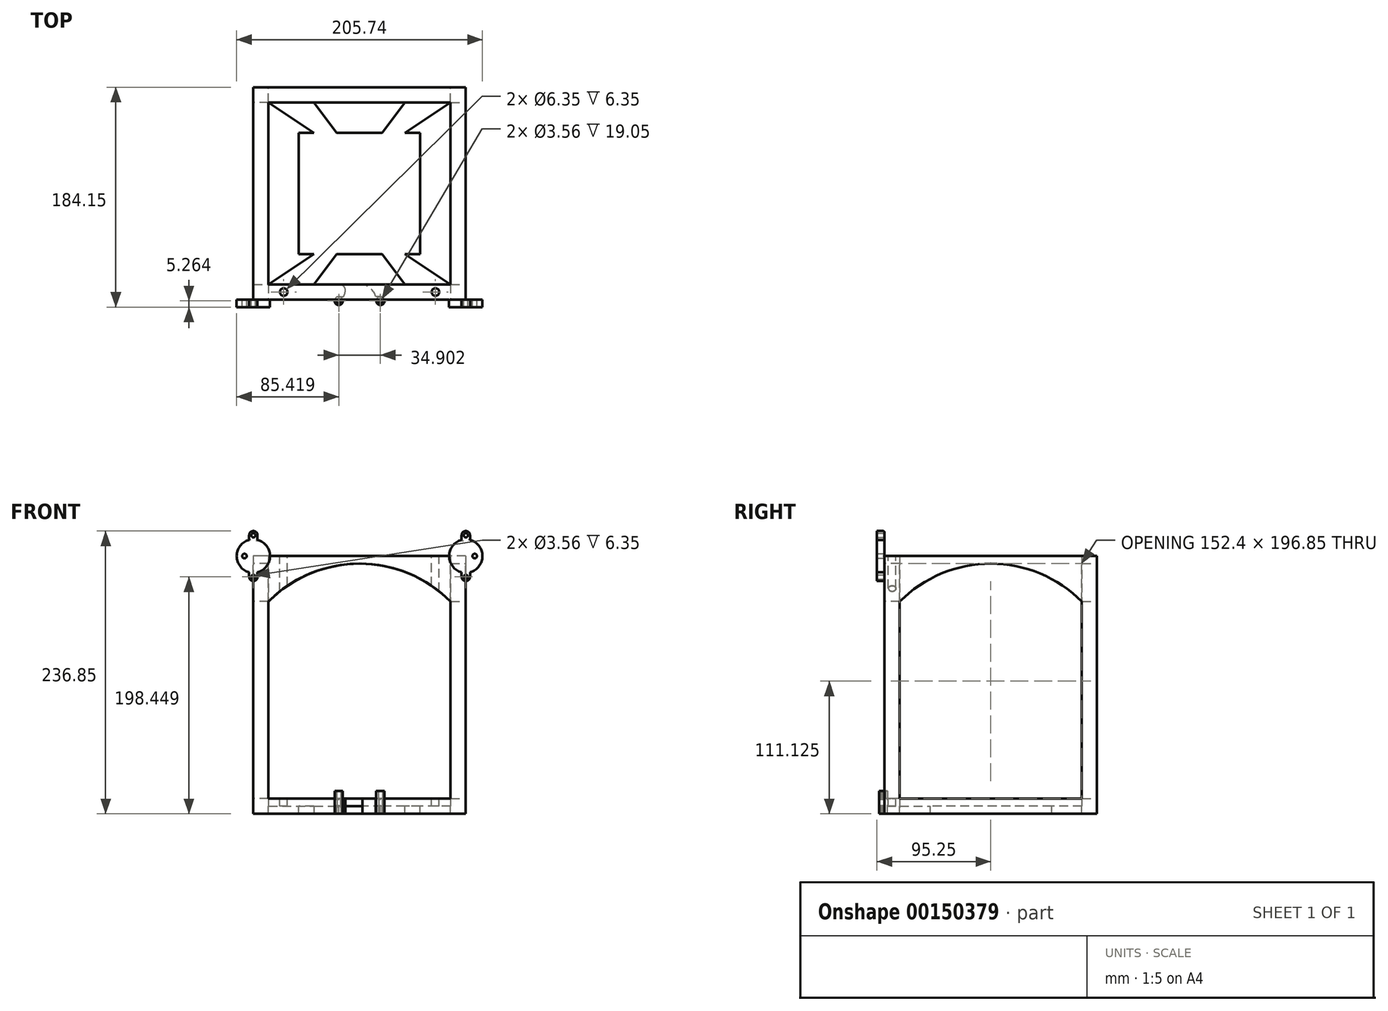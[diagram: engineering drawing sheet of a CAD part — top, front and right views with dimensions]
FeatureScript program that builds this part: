
annotation { "Feature Type Name" : "Feature", "Feature Type Description" : "" }
export const myFeature = defineFeature(function(context is Context, id is Id, definition is map)
    precondition{}
    {
        {
            var Q0;
            Q0=qCreatedBy(makeId("Top.planeOp"),FACE);
            var sketch = newSketch(context, id + "F0", { "sketchPlane" : qUnion([Q0])});
            skLineSegment(sketch, "E0.bottom", {"start": v(50.8, 50.8) * mm, "end": v(-50.8, 50.8) * mm});
            skLineSegment(sketch, "E0.top", {"start": v(50.8, -50.8) * mm, "end": v(-50.8, -50.8) * mm});
            skLineSegment(sketch, "E0.left", {"start": v(50.8, 50.8) * mm, "end": v(50.8, -50.8) * mm});
            skLineSegment(sketch, "E0.right", {"start": v(-50.8, 50.8) * mm, "end": v(-50.8, -50.8) * mm});
            skPoint(sketch, "E0.middle", {"position": v(0, 0) * mm});
            skSolve(sketch);
        }
        {
            var Q0;
            Q0 = qSketchRegion(id + "F0", true);
            extrude(context, id + "F1", {"entities" : qUnion([Q0]), "oppositeDirection" : true, "depth" : 6.35 * mm});
        }
        {
            var Q0;
            Q0=qCreatedBy(makeId("Right.planeOp"),FACE);
            var sketch = newSketch(context, id + "F2", { "sketchPlane" : qUnion([Q0])});
            skLineSegment(sketch, "E1.bottom", {"start": v(-76.2, 6.35) * mm, "end": v(-88.9, 6.35) * mm});
            skLineSegment(sketch, "E1.top", {"start": v(-76.2, -6.35) * mm, "end": v(-88.9, -6.35) * mm});
            skLineSegment(sketch, "E1.left", {"start": v(-76.2, 6.35) * mm, "end": v(-76.2, -6.35) * mm});
            skLineSegment(sketch, "E1.right", {"start": v(-88.9, 6.35) * mm, "end": v(-88.9, -6.35) * mm});
            skPoint(sketch, "E1.middle", {"position": v(-82.55, 0) * mm});
            skSolve(sketch);
        }
        {
            var Q0;
            Q0 = qSketchRegion(id + "F2", true);
            extrude(context, id + "F3", {"entities" : qUnion([Q0]), "endBound" : BoundingType.SYMMETRIC, "depth" : 177.8 * mm});
        }
        {
            var Q0;
            Q0=makeQuery(id+"F3.opExtrude","SWEPT_BODY",BODY,{"disambiguationData":[OSD([sQuery(id+"F2.wireOp",EDGE,"E1.bottom"),sQuery(id+"F2.wireOp",EDGE,"E1.top"),sQuery(id+"F2.wireOp",EDGE,"E1.left"),sQuery(id+"F2.wireOp",EDGE,"E1.right")])]});
            var Q1;
            Q1=qCreatedBy(makeId("Front.planeOp"),FACE);
            mirror(context, id + "F4", {"entities" : qUnion([Q0]), "mirrorPlane" : qUnion([Q1])});
        }
        {
            var Q0;
            Q0=qCreatedBy(makeId("Front.planeOp"),FACE);
            var sketch = newSketch(context, id + "F5", { "sketchPlane" : qUnion([Q0])});
            skLineSegment(sketch, "E2", {"start": v(76.2, 6.35) * mm, "end": v(76.2, -6.35) * mm});
            skLineSegment(sketch, "E3", {"start": v(76.2, -6.35) * mm, "end": v(88.9, -6.35) * mm});
            skLineSegment(sketch, "E4", {"start": v(88.9, -6.35) * mm, "end": v(88.9, 6.35) * mm});
            skLineSegment(sketch, "E5", {"start": v(88.9, 6.35) * mm, "end": v(76.2, 6.35) * mm});
            skSolve(sketch);
        }
        {
            var Q0;
            Q0 = qSketchRegion(id + "F5", true);
            extrude(context, id + "F6", {"entities" : qUnion([Q0]), "endBound" : BoundingType.SYMMETRIC, "depth" : 152.4 * mm});
        }
        {
            var Q0;
            Q0=makeQuery(id+"F6.opExtrude","SWEPT_BODY",BODY,{"disambiguationData":[OSD([sQuery(id+"F5.wireOp",EDGE,"E2"),sQuery(id+"F5.wireOp",EDGE,"E3"),sQuery(id+"F5.wireOp",EDGE,"E4"),sQuery(id+"F5.wireOp",EDGE,"E5")])]});
            var Q1;
            Q1=qCreatedBy(makeId("Right.planeOp"),FACE);
            mirror(context, id + "F7", {"entities" : qUnion([Q0]), "mirrorPlane" : qUnion([Q1])});
        }
        {
            var Q0;
            Q0=makeQuery(id+"F1.opExtrude","SWEPT_FACE",FACE,{"disambiguationData":[OSD([sQuery(id+"F0.wireOp",EDGE,"E0.top")])]});
            var sketch = newSketch(context, id + "F8", { "sketchPlane" : qUnion([Q0])});
            skLineSegment(sketch, "E6", {"start": v(-38.1, 0) * mm, "end": v(-38.1, -6.35) * mm});
            skLineSegment(sketch, "E7", {"start": v(-38.1, -6.35) * mm, "end": v(-19.05, -6.35) * mm});
            skLineSegment(sketch, "E8", {"start": v(-19.05, -6.35) * mm, "end": v(-19.05, 0) * mm});
            skLineSegment(sketch, "E9", {"start": v(-19.05, 0) * mm, "end": v(-38.1, 0) * mm});
            skLineSegment(sketch, "E10.MirrorCS", {"start": v(19.05, -6.35) * mm, "end": v(19.05, 0) * mm, "construction": true});
            skLineSegment(sketch, "E11.MirrorCS", {"start": v(19.05, 0) * mm, "end": v(38.1, 0) * mm, "construction": true});
            skLineSegment(sketch, "E12.MirrorCS", {"start": v(38.1, 0) * mm, "end": v(38.1, -6.35) * mm, "construction": true});
            skLineSegment(sketch, "E13.MirrorCS", {"start": v(38.1, -6.35) * mm, "end": v(19.05, -6.35) * mm, "construction": true});
            skSolve(sketch);
        }
        {
            var Q0;
            Q0=makeQuery(id+"F3.opExtrude","SWEPT_FACE",FACE,{"disambiguationData":[OSD([sQuery(id+"F2.wireOp",EDGE,"E1.left")])]});
            var sketch = newSketch(context, id + "F9", { "sketchPlane" : qUnion([Q0])});
            skLineSegment(sketch, "E14.bottom", {"start": v(-76.2, -6.35) * mm, "end": v(-38.1, -6.35) * mm, "construction": true});
            skLineSegment(sketch, "E14.top", {"start": v(-76.2, 0) * mm, "end": v(-38.1, 0) * mm, "construction": true});
            skLineSegment(sketch, "E14.left", {"start": v(-76.2, -6.35) * mm, "end": v(-76.2, 0) * mm, "construction": true});
            skLineSegment(sketch, "E14.right", {"start": v(-38.1, -6.35) * mm, "end": v(-38.1, 0) * mm, "construction": true});
            skLineSegment(sketch, "E15.MirrorCS", {"start": v(76.2, 0) * mm, "end": v(38.1, 0) * mm});
            skLineSegment(sketch, "E16.MirrorCS", {"start": v(38.1, -6.35) * mm, "end": v(38.1, 0) * mm});
            skLineSegment(sketch, "E17.MirrorCS", {"start": v(76.2, -6.35) * mm, "end": v(38.1, -6.35) * mm});
            skLineSegment(sketch, "E18.MirrorCS", {"start": v(76.2, -6.35) * mm, "end": v(76.2, 0) * mm});
            skSolve(sketch);
        }
        {
            var Q0;
            Q0=makeQuery(id+"F9.imprint","IMPRINT",FACE,{"disambiguationData":[TD([[makeQuery(id+"F9.imprint","IMPRINT",EDGE,{"derivedFrom":sQuery(id+"F9.wireOp",EDGE,"E15.MirrorCS")}),1.0]])]});
            var Q1;
            Q1=makeQuery(id+"F8.imprint","IMPRINT",FACE,{"disambiguationData":[TD([[makeQuery(id+"F8.imprint","IMPRINT",EDGE,{"derivedFrom":sQuery(id+"F8.wireOp",EDGE,"E6")}),1.0]])]});
            loft(context, id + "F10", {"sheetProfilesArray" : [{ "sheetProfileEntities" : qUnion([Q0]) }, { "sheetProfileEntities" : qUnion([Q1]) }]});
        }
        {
            var Q0;
            Q0=makeQuery(id+"F10.opLoft","SWEPT_BODY",BODY,{"disambiguationData":[OSD([makeQuery(id+"F8.imprint","IMPRINT",FACE,{"disambiguationData":[TD([[makeQuery(id+"F8.imprint","IMPRINT",EDGE,{"derivedFrom":sQuery(id+"F8.wireOp",EDGE,"E6")}),1.0]])]}),makeQuery(id+"F9.imprint","IMPRINT",FACE,{"disambiguationData":[TD([[makeQuery(id+"F9.imprint","IMPRINT",EDGE,{"derivedFrom":sQuery(id+"F9.wireOp",EDGE,"E15.MirrorCS")}),1.0]])]})])]});
            var Q1;
            Q1=qCreatedBy(makeId("Right.planeOp"),FACE);
            mirror(context, id + "F11", {"entities" : qUnion([Q0]), "mirrorPlane" : qUnion([Q1])});
        }
        {
            var Q0;
            Q0=makeQuery(id+"F11.opPattern","COPY",BODY,{"derivedFrom":makeQuery(id+"F10.opLoft","SWEPT_BODY",BODY,{"disambiguationData":[OSD([makeQuery(id+"F8.imprint","IMPRINT",FACE,{"disambiguationData":[TD([[makeQuery(id+"F8.imprint","IMPRINT",EDGE,{"derivedFrom":sQuery(id+"F8.wireOp",EDGE,"E6")}),1.0]])]}),makeQuery(id+"F9.imprint","IMPRINT",FACE,{"disambiguationData":[TD([[makeQuery(id+"F9.imprint","IMPRINT",EDGE,{"derivedFrom":sQuery(id+"F9.wireOp",EDGE,"E15.MirrorCS")}),1.0]])]})])]}),"instanceName":"1"});
            var Q1;
            Q1=makeQuery(id+"F10.opLoft","SWEPT_BODY",BODY,{"disambiguationData":[OSD([makeQuery(id+"F8.imprint","IMPRINT",FACE,{"disambiguationData":[TD([[makeQuery(id+"F8.imprint","IMPRINT",EDGE,{"derivedFrom":sQuery(id+"F8.wireOp",EDGE,"E6")}),1.0]])]}),makeQuery(id+"F9.imprint","IMPRINT",FACE,{"disambiguationData":[TD([[makeQuery(id+"F9.imprint","IMPRINT",EDGE,{"derivedFrom":sQuery(id+"F9.wireOp",EDGE,"E15.MirrorCS")}),1.0]])]})])]});
            var Q2;
            Q2=qCreatedBy(makeId("Front.planeOp"),FACE);
            mirror(context, id + "F12", {"entities" : qUnion([Q0, Q1]), "mirrorPlane" : qUnion([Q2])});
        }
        {
            var Q0;
            Q0=makeQuery(id+"F1.opExtrude","SWEPT_BODY",BODY,{"disambiguationData":[OSD([sQuery(id+"F0.wireOp",EDGE,"E0.bottom"),sQuery(id+"F0.wireOp",EDGE,"E0.top"),sQuery(id+"F0.wireOp",EDGE,"E0.left"),sQuery(id+"F0.wireOp",EDGE,"E0.right")])]});
            var Q1;
            Q1=makeQuery(id+"F7.opPattern","COPY",BODY,{"derivedFrom":makeQuery(id+"F6.opExtrude","SWEPT_BODY",BODY,{"disambiguationData":[OSD([sQuery(id+"F5.wireOp",EDGE,"E2"),sQuery(id+"F5.wireOp",EDGE,"E3"),sQuery(id+"F5.wireOp",EDGE,"E4"),sQuery(id+"F5.wireOp",EDGE,"E5")])]}),"instanceName":"1"});
            var Q2;
            Q2=makeQuery(id+"F12.opPattern","COPY",BODY,{"derivedFrom":makeQuery(id+"F10.opLoft","SWEPT_BODY",BODY,{"disambiguationData":[OSD([makeQuery(id+"F8.imprint","IMPRINT",FACE,{"disambiguationData":[TD([[makeQuery(id+"F8.imprint","IMPRINT",EDGE,{"derivedFrom":sQuery(id+"F8.wireOp",EDGE,"E6")}),1.0]])]}),makeQuery(id+"F9.imprint","IMPRINT",FACE,{"disambiguationData":[TD([[makeQuery(id+"F9.imprint","IMPRINT",EDGE,{"derivedFrom":sQuery(id+"F9.wireOp",EDGE,"E15.MirrorCS")}),1.0]])]})])]}),"instanceName":"1"});
            var Q3;
            Q3=makeQuery(id+"F4.opPattern","COPY",BODY,{"derivedFrom":makeQuery(id+"F3.opExtrude","SWEPT_BODY",BODY,{"disambiguationData":[OSD([sQuery(id+"F2.wireOp",EDGE,"E1.bottom"),sQuery(id+"F2.wireOp",EDGE,"E1.top"),sQuery(id+"F2.wireOp",EDGE,"E1.left"),sQuery(id+"F2.wireOp",EDGE,"E1.right")])]}),"instanceName":"1"});
            var Q4;
            Q4=makeQuery(id+"F3.opExtrude","SWEPT_BODY",BODY,{"disambiguationData":[OSD([sQuery(id+"F2.wireOp",EDGE,"E1.bottom"),sQuery(id+"F2.wireOp",EDGE,"E1.top"),sQuery(id+"F2.wireOp",EDGE,"E1.left"),sQuery(id+"F2.wireOp",EDGE,"E1.right")])]});
            var Q5;
            Q5=makeQuery(id+"F6.opExtrude","SWEPT_BODY",BODY,{"disambiguationData":[OSD([sQuery(id+"F5.wireOp",EDGE,"E2"),sQuery(id+"F5.wireOp",EDGE,"E3"),sQuery(id+"F5.wireOp",EDGE,"E4"),sQuery(id+"F5.wireOp",EDGE,"E5")])]});
            var Q6;
            Q6=makeQuery(id+"F11.opPattern","COPY",BODY,{"derivedFrom":makeQuery(id+"F10.opLoft","SWEPT_BODY",BODY,{"disambiguationData":[OSD([makeQuery(id+"F8.imprint","IMPRINT",FACE,{"disambiguationData":[TD([[makeQuery(id+"F8.imprint","IMPRINT",EDGE,{"derivedFrom":sQuery(id+"F8.wireOp",EDGE,"E6")}),1.0]])]}),makeQuery(id+"F9.imprint","IMPRINT",FACE,{"disambiguationData":[TD([[makeQuery(id+"F9.imprint","IMPRINT",EDGE,{"derivedFrom":sQuery(id+"F9.wireOp",EDGE,"E15.MirrorCS")}),1.0]])]})])]}),"instanceName":"1"});
            var Q7;
            Q7=makeQuery(id+"F10.opLoft","SWEPT_BODY",BODY,{"disambiguationData":[OSD([makeQuery(id+"F8.imprint","IMPRINT",FACE,{"disambiguationData":[TD([[makeQuery(id+"F8.imprint","IMPRINT",EDGE,{"derivedFrom":sQuery(id+"F8.wireOp",EDGE,"E6")}),1.0]])]}),makeQuery(id+"F9.imprint","IMPRINT",FACE,{"disambiguationData":[TD([[makeQuery(id+"F9.imprint","IMPRINT",EDGE,{"derivedFrom":sQuery(id+"F9.wireOp",EDGE,"E15.MirrorCS")}),1.0]])]})])]});
            var Q8;
            Q8=makeQuery(id+"F12.opPattern","COPY",BODY,{"derivedFrom":makeQuery(id+"F11.opPattern","COPY",BODY,{"derivedFrom":makeQuery(id+"F10.opLoft","SWEPT_BODY",BODY,{"disambiguationData":[OSD([makeQuery(id+"F8.imprint","IMPRINT",FACE,{"disambiguationData":[TD([[makeQuery(id+"F8.imprint","IMPRINT",EDGE,{"derivedFrom":sQuery(id+"F8.wireOp",EDGE,"E6")}),1.0]])]}),makeQuery(id+"F9.imprint","IMPRINT",FACE,{"disambiguationData":[TD([[makeQuery(id+"F9.imprint","IMPRINT",EDGE,{"derivedFrom":sQuery(id+"F9.wireOp",EDGE,"E15.MirrorCS")}),1.0]])]})])]}),"instanceName":"1"}),"instanceName":"1"});
            booleanBodies(context, id + "F13", {"operationType" : BooleanOperationType.UNION, "tools" : qUnion([Q0, Q1, Q2, Q3, Q4, Q5, Q6, Q7, Q8])});
        }
        {
            var Q0;
            {var subQ0=makeQuery(id+"F6.opExtrude","SWEPT_FACE",FACE,{"disambiguationData":[OSD([sQuery(id+"F5.wireOp",EDGE,"E5")])]});var subQ1=makeQuery(id+"F3.opExtrude","SWEPT_FACE",FACE,{"disambiguationData":[OSD([sQuery(id+"F2.wireOp",EDGE,"E1.bottom")])]});Q0=makeQuery(id+"F13.opBoolean","MERGE",FACE,{"derivedFrom":[subQ1,makeQuery(id+"F4.opPattern","COPY",FACE,{"derivedFrom":subQ1,"instanceName":"1"}),subQ0,makeQuery(id+"F7.opPattern","COPY",FACE,{"derivedFrom":subQ0,"instanceName":"1"})]});}
            var sketch = newSketch(context, id + "F14", { "sketchPlane" : qUnion([Q0])});
            skLineSegment(sketch, "E19.bottom", {"start": v(-76.2, 76.2) * mm, "end": v(-88.9, 76.2) * mm});
            skLineSegment(sketch, "E19.top", {"start": v(-76.2, 88.9) * mm, "end": v(-88.9, 88.9) * mm});
            skLineSegment(sketch, "E19.left", {"start": v(-76.2, 76.2) * mm, "end": v(-76.2, 88.9) * mm});
            skLineSegment(sketch, "E19.right", {"start": v(-88.9, 76.2) * mm, "end": v(-88.9, 88.9) * mm});
            skLineSegment(sketch, "E20.bottom", {"start": v(76.2, 76.2) * mm, "end": v(88.9, 76.2) * mm});
            skLineSegment(sketch, "E20.top", {"start": v(76.2, 88.9) * mm, "end": v(88.9, 88.9) * mm});
            skLineSegment(sketch, "E20.left", {"start": v(76.2, 76.2) * mm, "end": v(76.2, 88.9) * mm});
            skLineSegment(sketch, "E20.right", {"start": v(88.9, 76.2) * mm, "end": v(88.9, 88.9) * mm});
            skLineSegment(sketch, "E21.bottom", {"start": v(76.2, -76.2) * mm, "end": v(88.9, -76.2) * mm});
            skLineSegment(sketch, "E21.top", {"start": v(76.2, -88.9) * mm, "end": v(88.9, -88.9) * mm});
            skLineSegment(sketch, "E21.left", {"start": v(76.2, -76.2) * mm, "end": v(76.2, -88.9) * mm});
            skLineSegment(sketch, "E21.right", {"start": v(88.9, -76.2) * mm, "end": v(88.9, -88.9) * mm});
            skLineSegment(sketch, "E22.bottom", {"start": v(-88.9, -88.9) * mm, "end": v(-76.2, -88.9) * mm});
            skLineSegment(sketch, "E22.top", {"start": v(-88.9, -76.2) * mm, "end": v(-76.2, -76.2) * mm});
            skLineSegment(sketch, "E22.left", {"start": v(-88.9, -88.9) * mm, "end": v(-88.9, -76.2) * mm});
            skLineSegment(sketch, "E22.right", {"start": v(-76.2, -88.9) * mm, "end": v(-76.2, -76.2) * mm});
            skSolve(sketch);
        }
        {
            var Q0;
            Q0 = qSketchRegion(id + "F14", true);
            extrude(context, id + "F15", {"entities" : qUnion([Q0]), "operationType" : NewBodyOperationType.ADD, "depth" : 203.2 * mm});
        }
        {
            var Q0;
            {var subQ0=makeQuery(id+"F3.opExtrude","CAP_FACE",FACE,{"disambiguationData":[OSD([sQuery(id+"F2.wireOp",EDGE,"E1.bottom"),sQuery(id+"F2.wireOp",EDGE,"E1.top"),sQuery(id+"F2.wireOp",EDGE,"E1.left"),sQuery(id+"F2.wireOp",EDGE,"E1.right")])],"isStart":true});Q0=makeQuery(id+"F15.boolean.opBoolean","MERGE",FACE,{"derivedFrom":[makeQuery(id+"F13.opBoolean","MERGE",FACE,{"derivedFrom":[subQ0,makeQuery(id+"F4.opPattern","COPY",FACE,{"derivedFrom":subQ0,"instanceName":"1"}),makeQuery(id+"F7.opPattern","COPY",FACE,{"derivedFrom":makeQuery(id+"F6.opExtrude","SWEPT_FACE",FACE,{"disambiguationData":[OSD([sQuery(id+"F5.wireOp",EDGE,"E4")])]}),"instanceName":"1"})]}),makeQuery(id+"F15.opExtrude","SWEPT_FACE",FACE,{"disambiguationData":[OSD([sQuery(id+"F14.wireOp",EDGE,"E19.right")])]}),makeQuery(id+"F15.opExtrude","SWEPT_FACE",FACE,{"disambiguationData":[OSD([sQuery(id+"F14.wireOp",EDGE,"E22.left")])]})]});}
            var sketch = newSketch(context, id + "F16", { "sketchPlane" : qUnion([Q0])});
            skArc(sketch, "E23", {"start": v(76.2, 171.45) * mm, "mid": v(0, 203.2) * mm, "end": v(-76.2, 171.45) * mm});
            skLineSegment(sketch, "E24", {"start": v(-76.2, 209.55) * mm, "end": v(76.2, 209.55) * mm});
            skLineSegment(sketch, "E25", {"start": v(76.2, 209.55) * mm, "end": v(76.2, 171.45) * mm});
            skLineSegment(sketch, "E26", {"start": v(-76.2, 209.55) * mm, "end": v(-76.2, 171.45) * mm});
            skSolve(sketch);
        }
        {
            var Q0;
            Q0 = qSketchRegion(id + "F16", true);
            extrude(context, id + "F17", {"entities" : qUnion([Q0]), "oppositeDirection" : true, "depth" : 12.7 * mm});
        }
        {
            var Q0;
            Q0=makeQuery(id+"F17.opExtrude","SWEPT_BODY",BODY,{"disambiguationData":[OSD([sQuery(id+"F16.wireOp",EDGE,"E23"),sQuery(id+"F16.wireOp",EDGE,"E24"),sQuery(id+"F16.wireOp",EDGE,"E25"),sQuery(id+"F16.wireOp",EDGE,"E26")])]});
            var Q1;
            Q1=qCreatedBy(makeId("Right.planeOp"),FACE);
            mirror(context, id + "F18", {"operationType" : NewBodyOperationType.ADD, "entities" : qUnion([Q0]), "mirrorPlane" : qUnion([Q1])});
        }
        {
            var Q0;
            Q0=makeQuery(id+"F15.boolean.opBoolean","MERGE",FACE,{"derivedFrom":[makeQuery(id+"F4.opPattern","COPY",FACE,{"derivedFrom":makeQuery(id+"F3.opExtrude","SWEPT_FACE",FACE,{"disambiguationData":[OSD([sQuery(id+"F2.wireOp",EDGE,"E1.right")])]}),"instanceName":"1"}),makeQuery(id+"F15.opExtrude","SWEPT_FACE",FACE,{"disambiguationData":[OSD([sQuery(id+"F14.wireOp",EDGE,"E19.top")])]}),makeQuery(id+"F15.opExtrude","SWEPT_FACE",FACE,{"disambiguationData":[OSD([sQuery(id+"F14.wireOp",EDGE,"E20.top")])]})]});
            var sketch = newSketch(context, id + "F19", { "sketchPlane" : qUnion([Q0])});
            skArc(sketch, "E27", {"start": v(76.2, 171.45) * mm, "mid": v(0, 203.2) * mm, "end": v(-76.2, 171.45) * mm});
            skLineSegment(sketch, "E28", {"start": v(-76.2, 171.45) * mm, "end": v(-76.2, 209.55) * mm});
            skLineSegment(sketch, "E29", {"start": v(-76.2, 209.55) * mm, "end": v(76.2, 209.55) * mm});
            skLineSegment(sketch, "E30", {"start": v(76.2, 209.55) * mm, "end": v(76.2, 171.45) * mm});
            skSolve(sketch);
        }
        {
            var Q0;
            Q0 = qSketchRegion(id + "F19", true);
            extrude(context, id + "F20", {"entities" : qUnion([Q0]), "oppositeDirection" : true, "depth" : 12.7 * mm});
        }
        {
            var Q0;
            Q0=makeQuery(id+"F20.opExtrude","SWEPT_BODY",BODY,{"disambiguationData":[OSD([sQuery(id+"F19.wireOp",EDGE,"E27"),sQuery(id+"F19.wireOp",EDGE,"E28"),sQuery(id+"F19.wireOp",EDGE,"E29"),sQuery(id+"F19.wireOp",EDGE,"E30")])]});
            var Q1;
            Q1=qCreatedBy(makeId("Front.planeOp"),FACE);
            mirror(context, id + "F21", {"operationType" : NewBodyOperationType.ADD, "entities" : qUnion([Q0]), "mirrorPlane" : qUnion([Q1])});
        }
        {
            var Q0;
            {var subQ0=makeQuery(id+"F20.opExtrude","SWEPT_FACE",FACE,{"disambiguationData":[OSD([sQuery(id+"F19.wireOp",EDGE,"E29")])]});var subQ1=makeQuery(id+"F17.opExtrude","SWEPT_FACE",FACE,{"disambiguationData":[OSD([sQuery(id+"F16.wireOp",EDGE,"E24")])]});Q0=makeQuery(id+"F21.boolean.opBoolean","MERGE",FACE,{"derivedFrom":[makeQuery(id+"F18.boolean.opBoolean","MERGE",FACE,{"derivedFrom":[makeQuery(id+"F15.opExtrude","CAP_FACE",FACE,{"disambiguationData":[OSD([sQuery(id+"F14.wireOp",EDGE,"E19.bottom"),sQuery(id+"F14.wireOp",EDGE,"E19.top"),sQuery(id+"F14.wireOp",EDGE,"E19.left"),sQuery(id+"F14.wireOp",EDGE,"E19.right")])],"isStart":false}),makeQuery(id+"F15.opExtrude","CAP_FACE",FACE,{"disambiguationData":[OSD([sQuery(id+"F14.wireOp",EDGE,"E22.bottom"),sQuery(id+"F14.wireOp",EDGE,"E22.top"),sQuery(id+"F14.wireOp",EDGE,"E22.left"),sQuery(id+"F14.wireOp",EDGE,"E22.right")])],"isStart":false}),subQ1]}),makeQuery(id+"F18.boolean.opBoolean","MERGE",FACE,{"derivedFrom":[makeQuery(id+"F15.opExtrude","CAP_FACE",FACE,{"disambiguationData":[OSD([sQuery(id+"F14.wireOp",EDGE,"E20.bottom"),sQuery(id+"F14.wireOp",EDGE,"E20.top"),sQuery(id+"F14.wireOp",EDGE,"E20.left"),sQuery(id+"F14.wireOp",EDGE,"E20.right")])],"isStart":false}),makeQuery(id+"F15.opExtrude","CAP_FACE",FACE,{"disambiguationData":[OSD([sQuery(id+"F14.wireOp",EDGE,"E21.bottom"),sQuery(id+"F14.wireOp",EDGE,"E21.top"),sQuery(id+"F14.wireOp",EDGE,"E21.left"),sQuery(id+"F14.wireOp",EDGE,"E21.right")])],"isStart":false}),makeQuery(id+"F18.opPattern","COPY",FACE,{"derivedFrom":subQ1,"instanceName":"1"})]}),subQ0,makeQuery(id+"F21.opPattern","COPY",FACE,{"derivedFrom":subQ0,"instanceName":"1"})]});}
            var sketch = newSketch(context, id + "F22", { "sketchPlane" : qUnion([Q0])});
            skCircle(sketch, "E31", {"center": v(-63.5, -82.55) * mm, "radius": 3.18 * mm});
            skCircle(sketch, "E32", {"center": v(63.5, -82.55) * mm, "radius": 3.18 * mm});
            skLineSegment(sketch, "E33", {"start": v(-63.5, -82.55) * mm, "end": v(63.5, -82.55) * mm, "construction": true});
            skLineSegment(sketch, "E34", {"start": v(63.5, -82.55) * mm, "end": v(0, 0) * mm, "construction": true});
            skLineSegment(sketch, "E35", {"start": v(0, 0) * mm, "end": v(-63.5, -82.55) * mm, "construction": true});
            skLineSegment(sketch, "E36", {"start": v(0, -76.2) * mm, "end": v(0, -82.55) * mm, "construction": true});
            skLineSegment(sketch, "E37", {"start": v(0, -82.55) * mm, "end": v(0, -88.9) * mm, "construction": true});
            skSolve(sketch);
        }
        {
            var Q0;
            Q0 = qSketchRegion(id + "F22", true);
            extrude(context, id + "F23", {"entities" : qUnion([Q0]), "operationType" : NewBodyOperationType.REMOVE, "oppositeDirection" : true, "depth" : 209.55 * mm});
        }
        {
            var Q0;
            {var subQ0=sQuery(id+"F2.wireOp",EDGE,"E1.top");var subQ1=sQuery(id+"F0.wireOp",EDGE,"E0.top");var subQ2=makeQuery(id+"F10.opLoft","SWEPT_FACE",FACE,{"disambiguationData":[OSD([subQ1,subQ0,sQuery(id+"F2.wireOp",EDGE,"E1.left"),sQuery(id+"F8.wireOp",EDGE,"E6"),sQuery(id+"F8.wireOp",EDGE,"E7"),sQuery(id+"F8.wireOp",EDGE,"E8"),sQuery(id+"F9.wireOp",EDGE,"E16.MirrorCS"),sQuery(id+"F9.wireOp",EDGE,"E17.MirrorCS"),sQuery(id+"F9.wireOp",EDGE,"E18.MirrorCS")])]});var subQ3=makeQuery(id+"F11.opPattern","COPY",FACE,{"derivedFrom":subQ2,"instanceName":"1"});var subQ4=makeQuery(id+"F6.opExtrude","SWEPT_FACE",FACE,{"disambiguationData":[OSD([sQuery(id+"F5.wireOp",EDGE,"E3")])]});var subQ5=makeQuery(id+"F3.opExtrude","SWEPT_FACE",FACE,{"disambiguationData":[OSD([subQ0])]});Q0=makeQuery(id+"F13.opBoolean","MERGE",FACE,{"derivedFrom":[makeQuery(id+"F1.opExtrude","CAP_FACE",FACE,{"disambiguationData":[OSD([sQuery(id+"F0.wireOp",EDGE,"E0.bottom"),subQ1,sQuery(id+"F0.wireOp",EDGE,"E0.left"),sQuery(id+"F0.wireOp",EDGE,"E0.right")])],"isStart":false}),subQ5,makeQuery(id+"F4.opPattern","COPY",FACE,{"derivedFrom":subQ5,"instanceName":"1"}),subQ4,makeQuery(id+"F7.opPattern","COPY",FACE,{"derivedFrom":subQ4,"instanceName":"1"}),subQ2,subQ3,makeQuery(id+"F12.opPattern","COPY",FACE,{"derivedFrom":subQ2,"instanceName":"1"}),makeQuery(id+"F12.opPattern","COPY",FACE,{"derivedFrom":subQ3,"instanceName":"1"})]});}
            var sketch = newSketch(context, id + "F24", { "sketchPlane" : qUnion([Q0])});
            skCircle(sketch, "E38", {"center": v(0, 82.55) * mm, "radius": 1.9 * mm});
            skArc(sketch, "E39", {"start": v(13.52, 93.49) * mm, "mid": v(0, 103.96) * mm, "end": v(-13.52, 93.49) * mm});
            skArc(sketch, "E40", {"start": v(17.45, 86.49) * mm, "mid": v(20.95, 89.99) * mm, "end": v(17.45, 93.49) * mm});
            skArc(sketch, "E41", {"start": v(-17.45, 93.49) * mm, "mid": v(-20.95, 89.99) * mm, "end": v(-17.45, 86.49) * mm});
            skLineSegment(sketch, "E42", {"start": v(17.45, 89.99) * mm, "end": v(0, 89.99) * mm, "construction": true});
            skLineSegment(sketch, "E43", {"start": v(0, 89.99) * mm, "end": v(-17.45, 89.99) * mm, "construction": true});
            skLineSegment(sketch, "E44", {"start": v(0, 82.55) * mm, "end": v(0, 76.02) * mm, "construction": true});
            skLineSegment(sketch, "E45", {"start": v(17.45, 89.99) * mm, "end": v(0, 82.55) * mm, "construction": true});
            skLineSegment(sketch, "E46", {"start": v(0, 82.55) * mm, "end": v(-17.45, 89.99) * mm, "construction": true});
            skLineSegment(sketch, "E47", {"start": v(17.45, 93.49) * mm, "end": v(13.52, 93.49) * mm});
            skLineSegment(sketch, "E48", {"start": v(17.45, 86.49) * mm, "end": v(13.52, 86.49) * mm});
            skLineSegment(sketch, "E49", {"start": v(17.45, 93.49) * mm, "end": v(17.45, 89.99) * mm, "construction": true});
            skLineSegment(sketch, "E50", {"start": v(17.45, 86.49) * mm, "end": v(17.45, 89.99) * mm, "construction": true});
            skLineSegment(sketch, "E51", {"start": v(-17.45, 93.49) * mm, "end": v(-13.52, 93.49) * mm});
            skLineSegment(sketch, "E52", {"start": v(-17.45, 86.49) * mm, "end": v(-13.52, 86.49) * mm});
            skLineSegment(sketch, "E53", {"start": v(-17.45, 93.49) * mm, "end": v(-17.45, 89.99) * mm, "construction": true});
            skLineSegment(sketch, "E54", {"start": v(-17.45, 89.99) * mm, "end": v(-17.45, 86.49) * mm, "construction": true});
            skArc(sketch, "E55.trimOffspring", {"start": v(-13.52, 86.49) * mm, "mid": v(0, 76.02) * mm, "end": v(13.52, 86.49) * mm});
            skCircle(sketch, "E56", {"center": v(17.45, 89.99) * mm, "radius": 1.78 * mm});
            skCircle(sketch, "E57.MirrorC", {"center": v(-17.45, 89.99) * mm, "radius": 1.78 * mm});
            skPoint(sketch, "E58", {"position": v(0, 88.9) * mm});
            skLineSegment(sketch, "E59", {"start": v(0, 88.9) * mm, "end": v(0, 82.55) * mm, "construction": true});
            skLineSegment(sketch, "E60", {"start": v(0, 82.55) * mm, "end": v(0, 76.2) * mm, "construction": true});
            skSolve(sketch);
        }
        {
            var Q0;
            Q0 = qSketchRegion(id + "F24", true);
            extrude(context, id + "F25", {"entities" : qUnion([Q0]), "operationType" : NewBodyOperationType.ADD, "oppositeDirection" : true, "depth" : 19.05 * mm});
        }
        {
            var Q0;
            Q0=makeQuery(id+"F25.opExtrude","CAP_FACE",FACE,{"disambiguationData":[OSD([sQuery(id+"F24.wireOp",EDGE,"E38"),sQuery(id+"F24.wireOp",EDGE,"E39"),sQuery(id+"F24.wireOp",EDGE,"E40"),sQuery(id+"F24.wireOp",EDGE,"E41"),sQuery(id+"F24.wireOp",EDGE,"E47"),sQuery(id+"F24.wireOp",EDGE,"E48"),sQuery(id+"F24.wireOp",EDGE,"E51"),sQuery(id+"F24.wireOp",EDGE,"E52"),sQuery(id+"F24.wireOp",EDGE,"E55.trimOffspring"),sQuery(id+"F24.wireOp",EDGE,"E56"),sQuery(id+"F24.wireOp",EDGE,"E57.MirrorC")])],"isStart":false});
            var sketch = newSketch(context, id + "F26", { "sketchPlane" : qUnion([Q0])});
            skArc(sketch, "E61", {"start": v(-13.97, -89.66) * mm, "mid": v(-13.97, -89.99) * mm, "end": v(-13.97, -90.31) * mm});
            skArc(sketch, "E62", {"start": v(-17.45, -93.49) * mm, "mid": v(-15.1, -92.57) * mm, "end": v(-13.97, -90.31) * mm});
            skArc(sketch, "E63", {"start": v(17.45, -86.49) * mm, "mid": v(13.95, -89.99) * mm, "end": v(17.45, -93.49) * mm});
            skLineSegment(sketch, "E64", {"start": v(-17.45, -86.49) * mm, "end": v(-13.52, -86.49) * mm});
            skLineSegment(sketch, "E65", {"start": v(-17.45, -93.49) * mm, "end": v(-13.52, -93.49) * mm});
            skLineSegment(sketch, "E66", {"start": v(17.45, -93.49) * mm, "end": v(13.52, -93.49) * mm});
            skLineSegment(sketch, "E67", {"start": v(13.52, -86.49) * mm, "end": v(17.45, -86.49) * mm});
            skArc(sketch, "E68.trimOffspring", {"start": v(-13.52, -93.49) * mm, "mid": v(0, -103.96) * mm, "end": v(13.52, -93.49) * mm});
            skArc(sketch, "E69.trimOffspring", {"start": v(13.52, -86.49) * mm, "mid": v(0, -76.02) * mm, "end": v(-13.52, -86.49) * mm});
            skArc(sketch, "E70.trimOffspring", {"start": v(-13.97, -89.66) * mm, "mid": v(-15.1, -87.4) * mm, "end": v(-17.45, -86.49) * mm});
            skSolve(sketch);
        }
        {
            var Q0;
            Q0 = qSketchRegion(id + "F26", true);
            extrude(context, id + "F27", {"entities" : qUnion([Q0]), "operationType" : NewBodyOperationType.REMOVE, "oppositeDirection" : true, "depth" : 25.4 * mm});
        }
        {
            var Q0;
            Q0=makeQuery(id+"F25.boolean.opBoolean","INTERSECT",EDGE,{"disambiguationData":[OD(1.0)],"derivedFrom":[makeQuery(id+"F3.opExtrude","SWEPT_FACE",FACE,{"disambiguationData":[OSD([sQuery(id+"F2.wireOp",EDGE,"E1.left")])]}),makeQuery(id+"F25.opExtrude","SWEPT_FACE",FACE,{"disambiguationData":[OSD([sQuery(id+"F24.wireOp",EDGE,"E55.trimOffspring")])]})]});
            var Q1;
            Q1=makeQuery(id+"F25.boolean.opBoolean","INTERSECT",EDGE,{"disambiguationData":[OD(0.0)],"derivedFrom":[makeQuery(id+"F3.opExtrude","SWEPT_FACE",FACE,{"disambiguationData":[OSD([sQuery(id+"F2.wireOp",EDGE,"E1.left")])]}),makeQuery(id+"F25.opExtrude","SWEPT_FACE",FACE,{"disambiguationData":[OSD([sQuery(id+"F24.wireOp",EDGE,"E55.trimOffspring")])]})]});
            fillet(context, id + "F28", {"entities" : qUnion([Q0, Q1]), "radius" : 5.08 * mm, "tangentPropagation" : true, "allowEdgeOverflow" : false});
        }
        {
            var Q0;
            {var subQ1=makeQuery(id+"F6.opExtrude","SWEPT_FACE",FACE,{"disambiguationData":[OSD([sQuery(id+"F5.wireOp",EDGE,"E4")])]});var subQ12=sQuery(id+"F2.wireOp",EDGE,"E1.right");var subQ16=sQuery(id+"F14.wireOp",EDGE,"E22.bottom");var subQ19=sQuery(id+"F19.wireOp",EDGE,"E29");var subQ30=sQuery(id+"F19.wireOp",EDGE,"E27");var subQ33=sQuery(id+"F14.wireOp",EDGE,"E21.top");Q0=makeQuery(id+"F25.boolean.opBoolean","SPLIT",FACE,{"disambiguationData":[TD([subQ1])],"derivedFrom":makeQuery(id+"F21.boolean.opBoolean","MERGE",FACE,{"derivedFrom":[makeQuery(id+"F15.boolean.opBoolean","MERGE",FACE,{"derivedFrom":[makeQuery(id+"F3.opExtrude","SWEPT_FACE",FACE,{"disambiguationData":[OSD([subQ12])]}),makeQuery(id+"F15.opExtrude","SWEPT_FACE",FACE,{"disambiguationData":[OSD([subQ33])]}),makeQuery(id+"F15.opExtrude","SWEPT_FACE",FACE,{"disambiguationData":[OSD([subQ16])]})]}),makeQuery(id+"F21.opPattern","COPY",FACE,{"derivedFrom":makeQuery(id+"F20.opExtrude","CAP_FACE",FACE,{"disambiguationData":[OSD([subQ30,sQuery(id+"F19.wireOp",EDGE,"E28"),subQ19,sQuery(id+"F19.wireOp",EDGE,"E30")])],"isStart":true}),"instanceName":"1"})]})});}
            var sketch = newSketch(context, id + "F29", { "sketchPlane" : qUnion([Q0])});
            skCircle(sketch, "E71", {"center": v(-96.34, 209.55) * mm, "radius": 1.9 * mm});
            skArc(sketch, "E72", {"start": v(-85.4, 196.03) * mm, "mid": v(-74.93, 209.55) * mm, "end": v(-85.4, 223.07) * mm});
            skArc(sketch, "E73", {"start": v(-92.4, 192.1) * mm, "mid": v(-88.9, 188.6) * mm, "end": v(-85.4, 192.1) * mm});
            skArc(sketch, "E74", {"start": v(-85.4, 227) * mm, "mid": v(-88.9, 230.5) * mm, "end": v(-92.4, 227) * mm});
            skLineSegment(sketch, "E75", {"start": v(-88.9, 192.1) * mm, "end": v(-88.9, 209.55) * mm, "construction": true});
            skLineSegment(sketch, "E76", {"start": v(-88.9, 209.55) * mm, "end": v(-88.9, 227) * mm, "construction": true});
            skLineSegment(sketch, "E77", {"start": v(-96.34, 209.55) * mm, "end": v(-102.87, 209.55) * mm, "construction": true});
            skLineSegment(sketch, "E78", {"start": v(-88.9, 192.1) * mm, "end": v(-96.34, 209.55) * mm, "construction": true});
            skLineSegment(sketch, "E79", {"start": v(-96.34, 209.55) * mm, "end": v(-88.9, 227) * mm, "construction": true});
            skLineSegment(sketch, "E80", {"start": v(-85.4, 192.1) * mm, "end": v(-85.4, 196.03) * mm});
            skLineSegment(sketch, "E81", {"start": v(-92.4, 192.1) * mm, "end": v(-92.4, 196.03) * mm});
            skLineSegment(sketch, "E82", {"start": v(-85.4, 192.1) * mm, "end": v(-88.9, 192.1) * mm, "construction": true});
            skLineSegment(sketch, "E83", {"start": v(-92.4, 192.1) * mm, "end": v(-88.9, 192.1) * mm, "construction": true});
            skLineSegment(sketch, "E84", {"start": v(-85.4, 227) * mm, "end": v(-85.4, 223.07) * mm});
            skLineSegment(sketch, "E85", {"start": v(-92.4, 227) * mm, "end": v(-92.4, 223.07) * mm});
            skLineSegment(sketch, "E86", {"start": v(-85.4, 227) * mm, "end": v(-88.9, 227) * mm, "construction": true});
            skLineSegment(sketch, "E87", {"start": v(-88.9, 227) * mm, "end": v(-92.4, 227) * mm, "construction": true});
            skArc(sketch, "E88.trimOffspring", {"start": v(-92.4, 223.07) * mm, "mid": v(-102.87, 209.55) * mm, "end": v(-92.4, 196.03) * mm});
            skCircle(sketch, "E89", {"center": v(-88.9, 192.1) * mm, "radius": 1.78 * mm});
            skCircle(sketch, "E90.MirrorC", {"center": v(-88.9, 227) * mm, "radius": 1.78 * mm});
            skCircle(sketch, "E91", {"center": v(96.34, 209.55) * mm, "radius": 1.9 * mm});
            skArc(sketch, "E92", {"start": v(85.4, 223.07) * mm, "mid": v(74.93, 209.55) * mm, "end": v(85.4, 196.03) * mm});
            skArc(sketch, "E93", {"start": v(92.4, 227) * mm, "mid": v(88.9, 230.5) * mm, "end": v(85.4, 227) * mm});
            skArc(sketch, "E94", {"start": v(85.4, 192.1) * mm, "mid": v(88.9, 188.6) * mm, "end": v(92.4, 192.1) * mm});
            skLineSegment(sketch, "E95", {"start": v(88.9, 227) * mm, "end": v(88.9, 209.55) * mm, "construction": true});
            skLineSegment(sketch, "E96", {"start": v(88.9, 209.55) * mm, "end": v(88.9, 192.1) * mm, "construction": true});
            skLineSegment(sketch, "E97", {"start": v(96.34, 209.55) * mm, "end": v(102.87, 209.55) * mm, "construction": true});
            skLineSegment(sketch, "E98", {"start": v(88.9, 227) * mm, "end": v(96.34, 209.55) * mm, "construction": true});
            skLineSegment(sketch, "E99", {"start": v(96.34, 209.55) * mm, "end": v(88.9, 192.1) * mm, "construction": true});
            skLineSegment(sketch, "E100", {"start": v(85.4, 227) * mm, "end": v(85.4, 223.07) * mm});
            skLineSegment(sketch, "E101", {"start": v(92.4, 227) * mm, "end": v(92.4, 223.07) * mm});
            skLineSegment(sketch, "E102", {"start": v(85.4, 227) * mm, "end": v(88.9, 227) * mm, "construction": true});
            skLineSegment(sketch, "E103", {"start": v(92.4, 227) * mm, "end": v(88.9, 227) * mm, "construction": true});
            skLineSegment(sketch, "E104", {"start": v(85.4, 192.1) * mm, "end": v(85.4, 196.03) * mm});
            skLineSegment(sketch, "E105", {"start": v(92.4, 192.1) * mm, "end": v(92.4, 196.03) * mm});
            skLineSegment(sketch, "E106", {"start": v(85.4, 192.1) * mm, "end": v(88.9, 192.1) * mm, "construction": true});
            skLineSegment(sketch, "E107", {"start": v(88.9, 192.1) * mm, "end": v(92.4, 192.1) * mm, "construction": true});
            skArc(sketch, "E108.trimOffspring", {"start": v(92.4, 196.03) * mm, "mid": v(102.87, 209.55) * mm, "end": v(92.4, 223.07) * mm});
            skCircle(sketch, "E109", {"center": v(88.9, 227) * mm, "radius": 1.78 * mm});
            skCircle(sketch, "E110.MirrorC", {"center": v(88.9, 192.1) * mm, "radius": 1.78 * mm});
            skSolve(sketch);
        }
        {
            var Q0;
            Q0 = qSketchRegion(id + "F29", true);
            extrude(context, id + "F30", {"entities" : qUnion([Q0]), "operationType" : NewBodyOperationType.ADD, "depth" : 6.35 * mm});
        }
        {
            var Q0;
            {var subQ0=sQuery(id+"F29.wireOp",EDGE,"E72");var subQ2=makeQuery(id+"F30.opExtrude","CAP_EDGE",EDGE,{"disambiguationData":[OSD([subQ0])],"isStart":true});Q0=qUnion([makeQuery(id+"F30.boolean.opBoolean","SPLIT",EDGE,{"disambiguationData":[topologyDisambiguationEdgeConnected([makeQuery(id+"F30.opExtrude","CAP_FACE",FACE,{"disambiguationData":[OSD([sQuery(id+"F29.wireOp",EDGE,"E71"),subQ0,sQuery(id+"F29.wireOp",EDGE,"E73"),sQuery(id+"F29.wireOp",EDGE,"E74"),sQuery(id+"F29.wireOp",EDGE,"E80"),sQuery(id+"F29.wireOp",EDGE,"E81"),sQuery(id+"F29.wireOp",EDGE,"E84"),sQuery(id+"F29.wireOp",EDGE,"E85"),sQuery(id+"F29.wireOp",EDGE,"E88.trimOffspring"),sQuery(id+"F29.wireOp",EDGE,"E89"),sQuery(id+"F29.wireOp",EDGE,"E90.MirrorC")])],"isStart":true})])],"derivedFrom":subQ2}),makeQuery(id+"F30.boolean.opBoolean","SPLIT",EDGE,{"disambiguationData":[topologyDisambiguationEdgeConnected([makeQuery(id+"F3.opExtrude","SWEPT_FACE",FACE,{"disambiguationData":[OSD([sQuery(id+"F2.wireOp",EDGE,"E1.right")])]})])],"derivedFrom":subQ2})]);}
            var Q1;
            Q1=makeQuery(id+"F30.opExtrude","CAP_EDGE",EDGE,{"disambiguationData":[OSD([sQuery(id+"F29.wireOp",EDGE,"E84")])],"isStart":true});
            var Q2;
            Q2=makeQuery(id+"F30.opExtrude","CAP_EDGE",EDGE,{"disambiguationData":[OSD([sQuery(id+"F29.wireOp",EDGE,"E80")])],"isStart":true});
            var Q3;
            {var subQ0=sQuery(id+"F29.wireOp",EDGE,"E92");var subQ2=makeQuery(id+"F30.opExtrude","CAP_EDGE",EDGE,{"disambiguationData":[OSD([subQ0])],"isStart":true});Q3=qUnion([makeQuery(id+"F30.boolean.opBoolean","SPLIT",EDGE,{"disambiguationData":[topologyDisambiguationEdgeConnected([makeQuery(id+"F30.opExtrude","CAP_FACE",FACE,{"disambiguationData":[OSD([sQuery(id+"F29.wireOp",EDGE,"E91"),subQ0,sQuery(id+"F29.wireOp",EDGE,"E93"),sQuery(id+"F29.wireOp",EDGE,"E94"),sQuery(id+"F29.wireOp",EDGE,"E100"),sQuery(id+"F29.wireOp",EDGE,"E101"),sQuery(id+"F29.wireOp",EDGE,"E104"),sQuery(id+"F29.wireOp",EDGE,"E105"),sQuery(id+"F29.wireOp",EDGE,"E108.trimOffspring"),sQuery(id+"F29.wireOp",EDGE,"E109"),sQuery(id+"F29.wireOp",EDGE,"E110.MirrorC")])],"isStart":true})])],"derivedFrom":subQ2}),makeQuery(id+"F30.boolean.opBoolean","SPLIT",EDGE,{"disambiguationData":[topologyDisambiguationEdgeConnected([makeQuery(id+"F3.opExtrude","SWEPT_FACE",FACE,{"disambiguationData":[OSD([sQuery(id+"F2.wireOp",EDGE,"E1.right")])]})])],"derivedFrom":subQ2})]);}
            var Q4;
            Q4=makeQuery(id+"F30.opExtrude","CAP_EDGE",EDGE,{"disambiguationData":[OSD([sQuery(id+"F29.wireOp",EDGE,"E100")])],"isStart":true});
            var Q5;
            Q5=makeQuery(id+"F30.opExtrude","CAP_EDGE",EDGE,{"disambiguationData":[OSD([sQuery(id+"F29.wireOp",EDGE,"E104")])],"isStart":true});
            fillet(context, id + "F31", {"entities" : qUnion([Q0, Q1, Q2, Q3, Q4, Q5]), "radius" : 1.27 * mm, "tangentPropagation" : true, "allowEdgeOverflow" : false});
        }
    });
